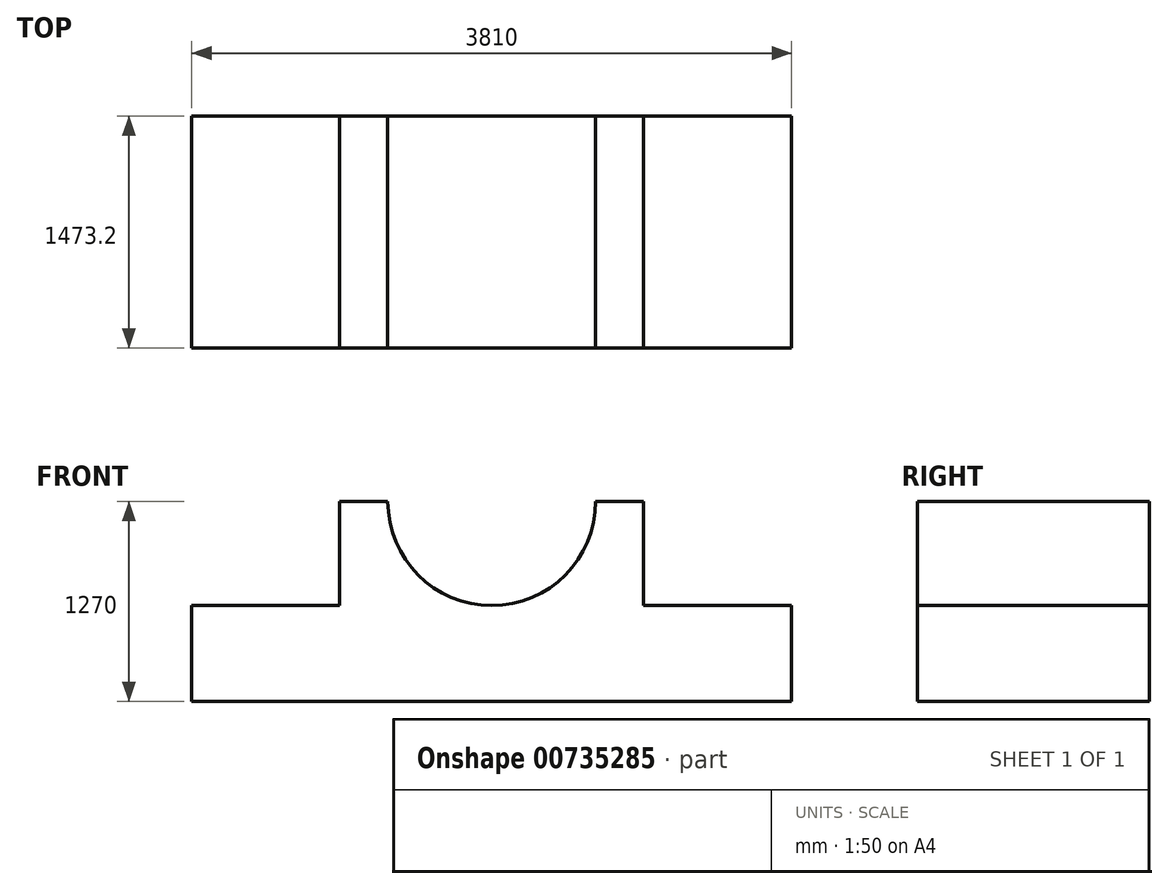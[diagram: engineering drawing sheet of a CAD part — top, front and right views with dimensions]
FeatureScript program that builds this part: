
annotation { "Feature Type Name" : "Feature", "Feature Type Description" : "" }
export const myFeature = defineFeature(function(context is Context, id is Id, definition is map)
    precondition{}
    {
        {
            var Q0;
            Q0=qCreatedBy(makeId("Front.planeOp"),FACE);
            var sketch = newSketch(context, id + "F0", { "sketchPlane" : qUnion([Q0])});
            skLineSegment(sketch, "E0", {"start": v(-1914.67, -19.39) * mm, "end": v(1895.33, -19.39) * mm});
            skLineSegment(sketch, "E1", {"start": v(-1914.67, -19.39) * mm, "end": v(-1914.67, 590.21) * mm});
            skLineSegment(sketch, "E2", {"start": v(1895.33, -19.39) * mm, "end": v(1895.33, 590.21) * mm});
            skLineSegment(sketch, "E3", {"start": v(-1914.67, 590.21) * mm, "end": v(-974.87, 590.21) * mm});
            skLineSegment(sketch, "E4", {"start": v(1895.33, 590.21) * mm, "end": v(955.53, 590.21) * mm});
            skLineSegment(sketch, "E5", {"start": v(-974.87, 590.21) * mm, "end": v(-974.87, 1250.61) * mm});
            skLineSegment(sketch, "E6", {"start": v(955.53, 590.21) * mm, "end": v(955.53, 1250.61) * mm});
            skLineSegment(sketch, "E7", {"start": v(-974.87, 1250.61) * mm, "end": v(-670.07, 1250.61) * mm});
            skLineSegment(sketch, "E8", {"start": v(-670.07, 1250.61) * mm, "end": v(-9.67, 1250.61) * mm});
            skCircle(sketch, "E9", {"center": v(-9.67, 1250.61) * mm, "radius": 660.4 * mm});
            skLineSegment(sketch, "E10", {"start": v(955.53, 1250.61) * mm, "end": v(650.73, 1250.61) * mm});
            skSolve(sketch);
        }
        {
            var Q0;
            Q0=makeQuery(id+"F0.imprint","IMPRINT",FACE,{"disambiguationData":[TD([[makeQuery(id+"F0.imprint","IMPRINT",EDGE,{"derivedFrom":sQuery(id+"F0.wireOp",EDGE,"E0")}),1.0]])]});
            extrude(context, id + "F1", {"entities" : qUnion([Q0]), "depth" : 1473.2 * mm, "offsetDistance" : 25.4 * mm});
        }
    });
